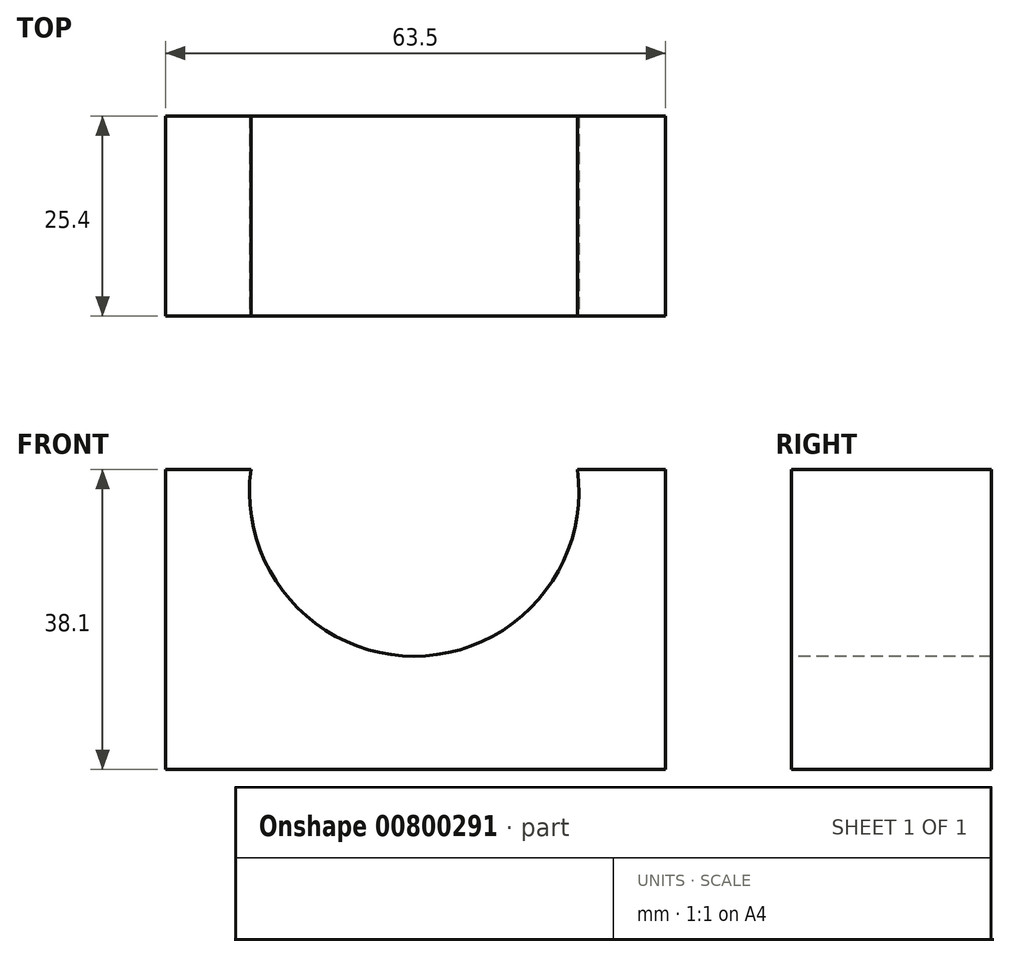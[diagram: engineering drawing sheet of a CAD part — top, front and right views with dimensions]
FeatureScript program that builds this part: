
annotation { "Feature Type Name" : "Feature", "Feature Type Description" : "" }
export const myFeature = defineFeature(function(context is Context, id is Id, definition is map)
    precondition{}
    {
        {
            var Q0;
            Q0=qCreatedBy(makeId("Front.planeOp"),FACE);
            var sketch = newSketch(context, id + "F0", { "sketchPlane" : qUnion([Q0])});
            skLineSegment(sketch, "E0", {"start": v(0, 0) * mm, "end": v(63.5, 0) * mm});
            skLineSegment(sketch, "E1", {"start": v(63.5, 0) * mm, "end": v(63.5, 38.1) * mm});
            skLineSegment(sketch, "E2", {"start": v(63.5, 38.1) * mm, "end": v(0, 38.1) * mm});
            skLineSegment(sketch, "E3", {"start": v(0, 38.1) * mm, "end": v(0, 0) * mm});
            skSolve(sketch);
        }
        {
            var Q0;
            Q0=makeQuery(id+"F0.imprint","IMPRINT",FACE,{"disambiguationData":[TD([[makeQuery(id+"F0.imprint","IMPRINT",EDGE,{"derivedFrom":sQuery(id+"F0.wireOp",EDGE,"E0")}),1.0]])]});
            extrude(context, id + "F1", {"entities" : qUnion([Q0]), "depth" : 25.4 * mm});
        }
        {
            var Q0;
            Q0=makeQuery(id+"F1.opExtrude","CAP_FACE",FACE,{"disambiguationData":[OSD([sQuery(id+"F0.wireOp",EDGE,"E0"),sQuery(id+"F0.wireOp",EDGE,"E1"),sQuery(id+"F0.wireOp",EDGE,"E2"),sQuery(id+"F0.wireOp",EDGE,"E3")])],"isStart":false});
            var sketch = newSketch(context, id + "F2", { "sketchPlane" : qUnion([Q0])});
            skArc(sketch, "E4", {"start": v(10.83, 38.1) * mm, "mid": v(31.57, 14.38) * mm, "end": v(52.3, 38.1) * mm});
            skSolve(sketch);
        }
        {
            var Q0;
            Q0=qSketchRegion(id+"F2",true);
            var Q1;
            {var subQ0=sQuery(id+"F2.wireOp",EDGE,"E4");Q1=makeQuery(id+"F2.imprint","IMPRINT",FACE,{"disambiguationData":[TD([[makeQuery(id+"F2.imprint","IMPRINT",EDGE,{"derivedFrom":subQ0}),1.0]])]});}
            extrude(context, id + "F3", {"entities" : qUnion([Q0, Q1]), "operationType" : NewBodyOperationType.REMOVE, "oppositeDirection" : true, "depth" : 25.4 * mm});
        }
    });
